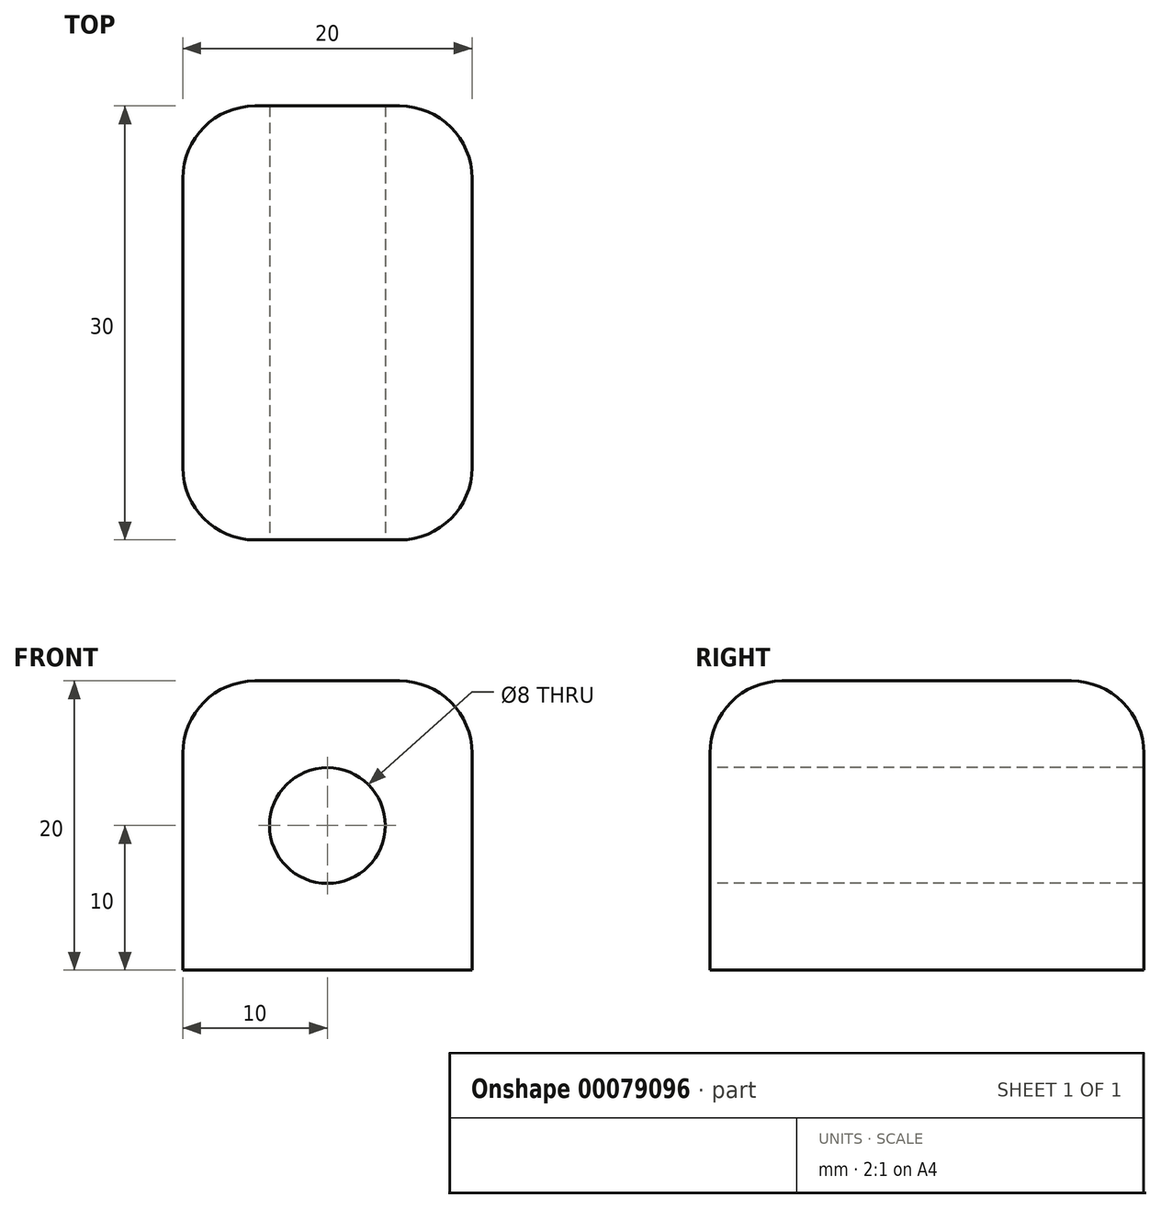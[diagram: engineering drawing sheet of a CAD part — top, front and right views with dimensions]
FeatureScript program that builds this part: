
annotation { "Feature Type Name" : "Feature", "Feature Type Description" : "" }
export const myFeature = defineFeature(function(context is Context, id is Id, definition is map)
    precondition{}
    {
        {
            var Q0;
            Q0=qCreatedBy(makeId("Right.planeOp"),FACE);
            var sketch = newSketch(context, id + "F0", { "sketchPlane" : qUnion([Q0])});
            skLineSegment(sketch, "E0", {"start": v(0, 0) * mm, "end": v(-30, 0) * mm});
            skLineSegment(sketch, "E1", {"start": v(-30, 0) * mm, "end": v(-30, 20) * mm});
            skLineSegment(sketch, "E2", {"start": v(-30, 20) * mm, "end": v(0, 20) * mm});
            skLineSegment(sketch, "E3", {"start": v(0, 20) * mm, "end": v(0, 0) * mm});
            skSolve(sketch);
        }
        {
            var Q0;
            Q0 = qSketchRegion(id + "F0", true);
            extrude(context, id + "F1", {"entities" : qUnion([Q0]), "endBound" : BoundingType.SYMMETRIC, "depth" : 20 * mm});
        }
        {
            var Q0;
            Q0=makeQuery(id+"F1.opExtrude","SWEPT_FACE",FACE,{"disambiguationData":[OSD([sQuery(id+"F0.wireOp",EDGE,"E1")])]});
            var sketch = newSketch(context, id + "F2", { "sketchPlane" : qUnion([Q0])});
            skLineSegment(sketch, "E4", {"start": v(-10, 10) * mm, "end": v(10, 10) * mm, "construction": true});
            skLineSegment(sketch, "E5", {"start": v(10, 10) * mm, "end": v(0, 20) * mm, "construction": true});
            skLineSegment(sketch, "E6", {"start": v(0, 20) * mm, "end": v(0, 0) * mm, "construction": true});
            skLineSegment(sketch, "E7", {"start": v(0, 0) * mm, "end": v(10, 10) * mm, "construction": true});
            skLineSegment(sketch, "E8", {"start": v(0, 0) * mm, "end": v(-10, 10) * mm, "construction": true});
            skLineSegment(sketch, "E9", {"start": v(0, 20) * mm, "end": v(-10, 10) * mm, "construction": true});
            skPoint(sketch, "E10", {"position": v(0, 10) * mm});
            skSolve(sketch);
        }
        {
            var Q0;
            Q0=sQuery(id+"F2.wireOp",VERTEX,"E10");
            var Q1;
            Q1=makeQuery(id+"F1.opExtrude","SWEPT_BODY",BODY,{"disambiguationData":[OSD([sQuery(id+"F0.wireOp",EDGE,"E0"),sQuery(id+"F0.wireOp",EDGE,"E1"),sQuery(id+"F0.wireOp",EDGE,"E2"),sQuery(id+"F0.wireOp",EDGE,"E3")])]});
            hole(context, id + "F3", {"style" : HoleStyle.SIMPLE, "endStyle" : HoleEndStyle.BLIND, "holeDiameter" : 8 * mm, "holeDepth" : 50 * mm, "locations" : qUnion([Q0]), "scope" : qUnion([Q1])});
        }
        {
            var Q0;
            Q0=makeQuery(id+"F1.opExtrude","SWEPT_EDGE",EDGE,{"disambiguationData":[OSD([sQuery(id+"F0.wireOp",EDGE,"E2"),sQuery(id+"F0.wireOp",EDGE,"E3")])]});
            var Q1;
            Q1=makeQuery(id+"F1.opExtrude","SWEPT_EDGE",EDGE,{"disambiguationData":[OSD([sQuery(id+"F0.wireOp",EDGE,"E1"),sQuery(id+"F0.wireOp",EDGE,"E2")])]});
            var Q2;
            Q2=makeQuery(id+"F1.opExtrude","CAP_EDGE",EDGE,{"disambiguationData":[OSD([sQuery(id+"F0.wireOp",EDGE,"E2")])],"isStart":true});
            var Q3;
            Q3=makeQuery(id+"F1.opExtrude","CAP_EDGE",EDGE,{"disambiguationData":[OSD([sQuery(id+"F0.wireOp",EDGE,"E2")])],"isStart":false});
            var Q4;
            Q4=makeQuery(id+"F1.opExtrude","CAP_EDGE",EDGE,{"disambiguationData":[OSD([sQuery(id+"F0.wireOp",EDGE,"E1")])],"isStart":false});
            var Q5;
            Q5=makeQuery(id+"F1.opExtrude","CAP_EDGE",EDGE,{"disambiguationData":[OSD([sQuery(id+"F0.wireOp",EDGE,"E1")])],"isStart":true});
            var Q6;
            Q6=makeQuery(id+"F1.opExtrude","CAP_EDGE",EDGE,{"disambiguationData":[OSD([sQuery(id+"F0.wireOp",EDGE,"E3")])],"isStart":false});
            var Q7;
            Q7=makeQuery(id+"F1.opExtrude","CAP_EDGE",EDGE,{"disambiguationData":[OSD([sQuery(id+"F0.wireOp",EDGE,"E3")])],"isStart":true});
            fillet(context, id + "F4", {"entities" : qUnion([Q0, Q1, Q2, Q3, Q4, Q5, Q6, Q7]), "radius" : 5 * mm, "tangentPropagation" : true, "allowEdgeOverflow" : false});
        }
    });
